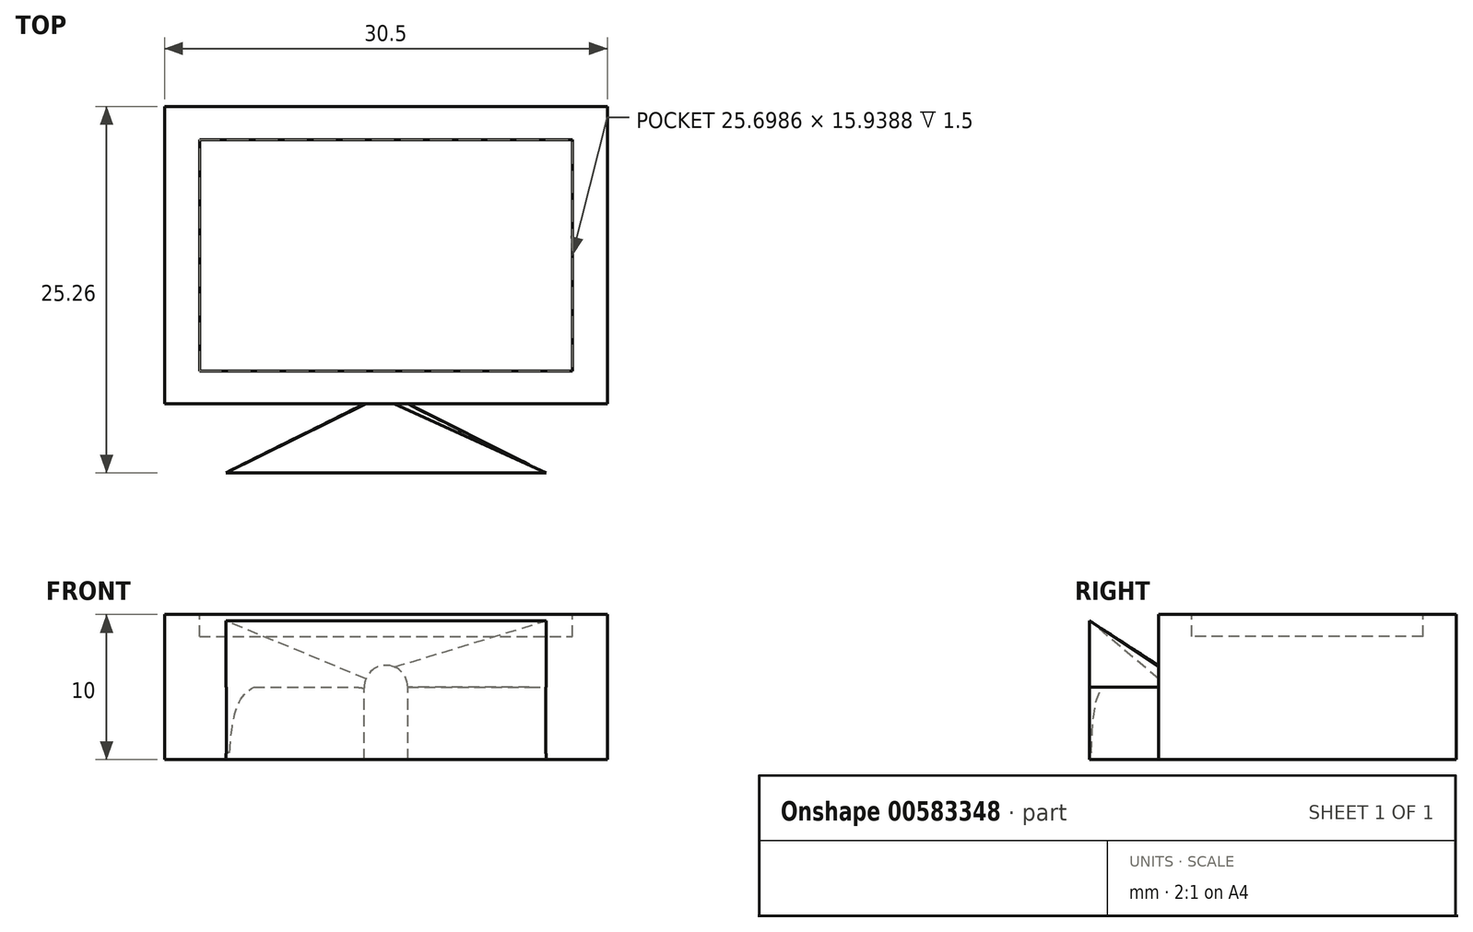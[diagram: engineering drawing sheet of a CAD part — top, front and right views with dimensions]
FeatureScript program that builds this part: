
annotation { "Feature Type Name" : "Feature", "Feature Type Description" : "" }
export const myFeature = defineFeature(function(context is Context, id is Id, definition is map)
    precondition{}
    {
        {
            var Q0;
            Q0=qCreatedBy(makeId("Top.planeOp"),FACE);
            var sketch = newSketch(context, id + "F0", { "sketchPlane" : qUnion([Q0])});
            skLineSegment(sketch, "E0.bottom", {"start": v(-15.25, 10.25) * mm, "end": v(15.25, 10.25) * mm});
            skLineSegment(sketch, "E0.top", {"start": v(-15.25, -10.25) * mm, "end": v(15.25, -10.25) * mm});
            skLineSegment(sketch, "E0.left", {"start": v(-15.25, 10.25) * mm, "end": v(-15.25, -10.25) * mm});
            skLineSegment(sketch, "E0.right", {"start": v(15.25, 10.25) * mm, "end": v(15.25, -10.25) * mm});
            skPoint(sketch, "E0.middle", {"position": v(0, 0) * mm});
            skSolve(sketch);
        }
        {
            var Q0;
            Q0=qSketchRegion(id+"F0",true);
            extrude(context, id + "F1", {"entities" : qUnion([Q0]), "depth" : 10 * mm, "offsetDistance" : 25 * mm});
        }
        {
            var Q0;
            Q0=makeQuery(id+"F1.opExtrude","CAP_FACE",FACE,{"disambiguationData":[OSD([sQuery(id+"F0.wireOp",EDGE,"E0.bottom"),sQuery(id+"F0.wireOp",EDGE,"E0.top"),sQuery(id+"F0.wireOp",EDGE,"E0.left"),sQuery(id+"F0.wireOp",EDGE,"E0.right")])],"isStart":false});
            var sketch = newSketch(context, id + "F2", { "sketchPlane" : qUnion([Q0])});
            skLineSegment(sketch, "E1.bottom", {"start": v(-12.85, 7.97) * mm, "end": v(12.85, 7.97) * mm});
            skLineSegment(sketch, "E1.top", {"start": v(-12.85, -7.97) * mm, "end": v(12.85, -7.97) * mm});
            skLineSegment(sketch, "E1.left", {"start": v(-12.85, 7.97) * mm, "end": v(-12.85, -7.97) * mm});
            skLineSegment(sketch, "E1.right", {"start": v(12.85, 7.97) * mm, "end": v(12.85, -7.97) * mm});
            skPoint(sketch, "E1.middle", {"position": v(0, 0) * mm});
            skSolve(sketch);
        }
        {
            var Q0;
            Q0=qSketchRegion(id+"F2",true);
            extrude(context, id + "F3", {"entities" : qUnion([Q0]), "operationType" : NewBodyOperationType.REMOVE, "oppositeDirection" : true, "depth" : 1.5 * mm, "offsetDistance" : 25 * mm});
        }
        {
            var Q0;
            Q0=makeQuery(id+"F1.opExtrude","SWEPT_FACE",FACE,{"disambiguationData":[OSD([sQuery(id+"F0.wireOp",EDGE,"E0.top")])]});
            var sketch = newSketch(context, id + "F4", { "sketchPlane" : qUnion([Q0])});
            skLineSegment(sketch, "E2", {"start": v(0, 5) * mm, "end": v(-1.5, 5) * mm});
            skPoint(sketch, "E2.startSnap0", {"position": v(15.25, 5) * mm});
            skCircle(sketch, "E3", {"center": v(0, 5) * mm, "radius": 1.5 * mm});
            skSolve(sketch);
        }
        {
            var Q0;
            Q0=qCreatedBy(makeId("Front.planeOp"),FACE);
            cPlane(context, id + "F5", {"entities" : qUnion([Q0]), "cplaneType" : CPlaneType.OFFSET, "offset" : 15 * mm, "width" : 150 * mm, "height" : 150 * mm});
        }
        {
            var Q0;
            Q0=qCreatedBy(id+"F5.planeOp",FACE);
            var sketch = newSketch(context, id + "F6", { "sketchPlane" : qUnion([Q0])});
            skLineSegment(sketch, "E4.bottom", {"start": v(-11.03, 9.57) * mm, "end": v(11.03, 9.57) * mm});
            skLineSegment(sketch, "E4.top", {"start": v(-11.03, 0.43) * mm, "end": v(11.03, 0.43) * mm});
            skLineSegment(sketch, "E4.left", {"start": v(-11.03, 9.57) * mm, "end": v(-11.03, 0.43) * mm});
            skLineSegment(sketch, "E4.right", {"start": v(11.03, 9.57) * mm, "end": v(11.03, 0.43) * mm});
            skPoint(sketch, "E4.middle", {"position": v(0, 5) * mm});
            skSolve(sketch);
        }
        {
            var Q1;
            Q1=makeQuery(id+"F4.imprint","IMPRINT",FACE,{"disambiguationData":[TD([[makeQuery(id+"F4.imprint","IMPRINT",EDGE,{"derivedFrom":sQuery(id+"F4.wireOp",EDGE,"E3")}),1.0]])]});
            var Q2;
            Q2=makeQuery(id+"F6.imprint","IMPRINT",FACE,{"disambiguationData":[TD([[makeQuery(id+"F6.imprint","IMPRINT",EDGE,{"derivedFrom":sQuery(id+"F6.wireOp",EDGE,"E4.bottom")}),-1.0]])]});
            loft(context, id + "F7", {"operationType" : NewBodyOperationType.ADD, "sheetProfilesArray" : [{ "sheetProfileEntities" : qUnion([Q1]) }, { "sheetProfileEntities" : qUnion([Q2]) }]});
        }
        {
            var Q0;
            Q0=qCreatedBy(makeId("Top.planeOp"),FACE);
            var sketch = newSketch(context, id + "F8", { "sketchPlane" : qUnion([Q0])});
            skLineSegment(sketch, "E5", {"start": v(-11.02, -15) * mm, "end": v(11.03, -15) * mm});
            skLineSegment(sketch, "E6", {"start": v(11.03, -15) * mm, "end": v(1.22, -10.1) * mm});
            skLineSegment(sketch, "E7", {"start": v(-11.02, -15) * mm, "end": v(-1.35, -10.17) * mm});
            skLineSegment(sketch, "E8", {"start": v(-1.35, -10.17) * mm, "end": v(1.22, -10.1) * mm});
            skSolve(sketch);
        }
        {
            var Q0;
            Q0 = qSketchRegion(id + "F8", true);
            extrude(context, id + "F9", {"entities" : qUnion([Q0]), "operationType" : NewBodyOperationType.ADD, "depth" : 5 * mm, "offsetDistance" : 25 * mm});
        }
    });
